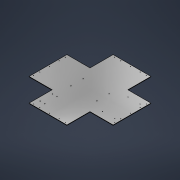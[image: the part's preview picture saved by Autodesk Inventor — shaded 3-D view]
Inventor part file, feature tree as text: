
AUTODESK INVENTOR PART (.ipt)
format: ipt  version: 2022.2 (Build 262287000, 287)  size: 203,776 bytes
history: native  units: in
note: dims shown in document units (in); Inventor stores cm internally (conversion verified against a paired STEP export)
features: reference x14, sketch x7, other x6, hole x4, sheet_metal_op x1
ambient origin geometry x8: Origin, YZ Plane, XZ Plane, XY Plane, X Axis, Y Axis, Z Axis, Center Point
bodies: Solid1 (feature_tree)
feature tree (32):
  parser-record x2  (decoder bookkeeping rows leaked as tree rows — omitted from the tree; the rows remain in map.json)
  sheet_metal_op  "Face1"
  hole  "Hole1"  [1 undecoded]
  sketch  "Sketch3"  dims[d4=0.5in d5=0.5in]
  sketch  "Sketch4"  dims[d6=0.5in d7=1.0in]
  hole  "Hole2"  [1 undecoded]
  hole  "Hole3"  [1 undecoded]
  hole  "Hole4"  [1 undecoded]
  sketch  "Sketch1"  dims[d0=27.5in d1=7.5625in]
  other  "Plate1"
  sketch  "Sketch2"  dims[d2=0.125in d3=0.5in]
  sketch  "Sketch5"  dims[d8=2.0in]
  reference  "Reference1"
  reference  "Reference2"
  reference  "Reference3"
  reference  "Reference4"
  sketch  "Sketch6"  dims[d9=1.0in]
  reference  "Reference5"
  reference  "Reference6"
  reference  "Reference7"
  reference  "Reference8"
  sketch  "Sketch8"  dims[d10=2.0in d11=1.0in d12=2.0in d13=1.0in d14=2.0in d15=0.161in d16=0.75in d17=0.375in d18=0.06in d19=0.5635in d20=0.125in d21=0.8108in d22=0.201in d23=0.75in d24=0.375in d25=0.19in d26=0.5635in d27=0.125in d28=0.8108in d29=0.201in d30=0.75in d31=0.375in d32=0.25in d33=0.5635in d34=1.0in d35=0.8108in d36=0.161in d37=0.75in d38=0.375in d39=0.06in d40=0.5635in d41=0.125in d42=0.8108in]
  reference  "Reference13"
  reference  "Reference14"
  reference  "Reference15"
  reference  "Reference16"
  reference  "Reference17"
  reference  "Reference18"
  other  "300127.iam"
  other  "PDH REV-11-1850:1"
  other  "Pneumatic Hub REV-11-1852:1"
note: 4 required parameter values undecoded (feature->parameter linkage not recoverable at this tier; creation-order binding heuristic only, values carry confidence <= 0.55)
note: 2 file-system paths scrubbed to <path> (originals preserved in map.json)
